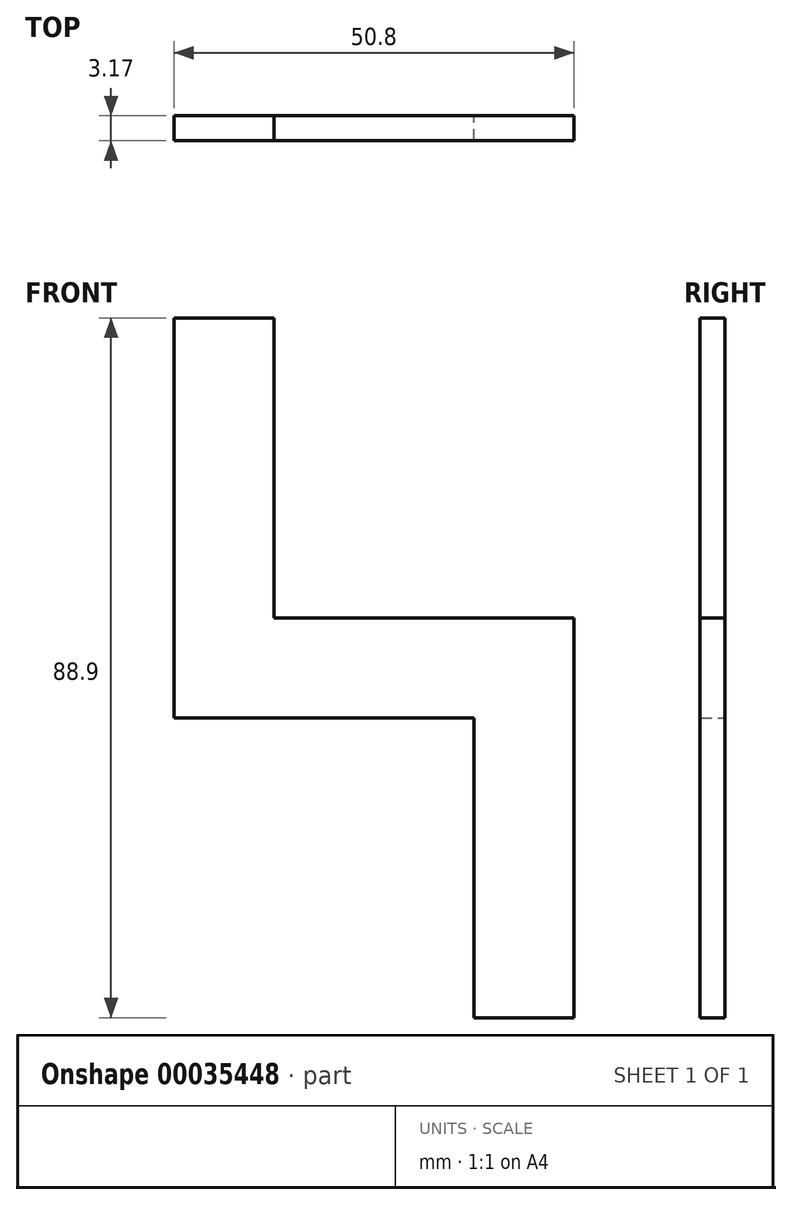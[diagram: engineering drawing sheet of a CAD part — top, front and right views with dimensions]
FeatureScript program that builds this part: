
annotation { "Feature Type Name" : "Feature", "Feature Type Description" : "" }
export const myFeature = defineFeature(function(context is Context, id is Id, definition is map)
    precondition{}
    {
        {
            var Q0;
            Q0=qCreatedBy(makeId("Front.planeOp"),FACE);
            var sketch = newSketch(context, id + "F0", { "sketchPlane" : qUnion([Q0])});
            skLineSegment(sketch, "E0.bottom", {"start": v(-25.4, 44.45) * mm, "end": v(-12.7, 44.45) * mm});
            skLineSegment(sketch, "E0.top", {"start": v(-25.4, -6.35) * mm, "end": v(-12.7, -6.35) * mm});
            skLineSegment(sketch, "E0.left", {"start": v(-25.4, 44.45) * mm, "end": v(-25.4, -6.35) * mm});
            skLineSegment(sketch, "E0.right", {"start": v(-12.7, 44.45) * mm, "end": v(-12.7, -6.35) * mm});
            skLineSegment(sketch, "E1.bottom", {"start": v(-25.4, 6.35) * mm, "end": v(25.4, 6.35) * mm});
            skLineSegment(sketch, "E1.top", {"start": v(-25.4, -6.35) * mm, "end": v(25.4, -6.35) * mm});
            skLineSegment(sketch, "E1.left", {"start": v(-25.4, 6.35) * mm, "end": v(-25.4, -6.35) * mm});
            skLineSegment(sketch, "E1.right", {"start": v(25.4, 6.35) * mm, "end": v(25.4, -6.35) * mm});
            skLineSegment(sketch, "E2.bottom", {"start": v(25.4, 6.35) * mm, "end": v(12.7, 6.35) * mm});
            skLineSegment(sketch, "E2.top", {"start": v(25.4, -44.45) * mm, "end": v(12.7, -44.45) * mm});
            skLineSegment(sketch, "E2.left", {"start": v(25.4, 6.35) * mm, "end": v(25.4, -44.45) * mm});
            skLineSegment(sketch, "E2.right", {"start": v(12.7, 6.35) * mm, "end": v(12.7, -44.45) * mm});
            skSolve(sketch);
        }
        {
            var Q0;
            Q0 = qSketchRegion(id + "F0", true);
            extrude(context, id + "F1", {"entities" : qUnion([Q0]), "depth" : 3.17 * mm});
        }
    });
